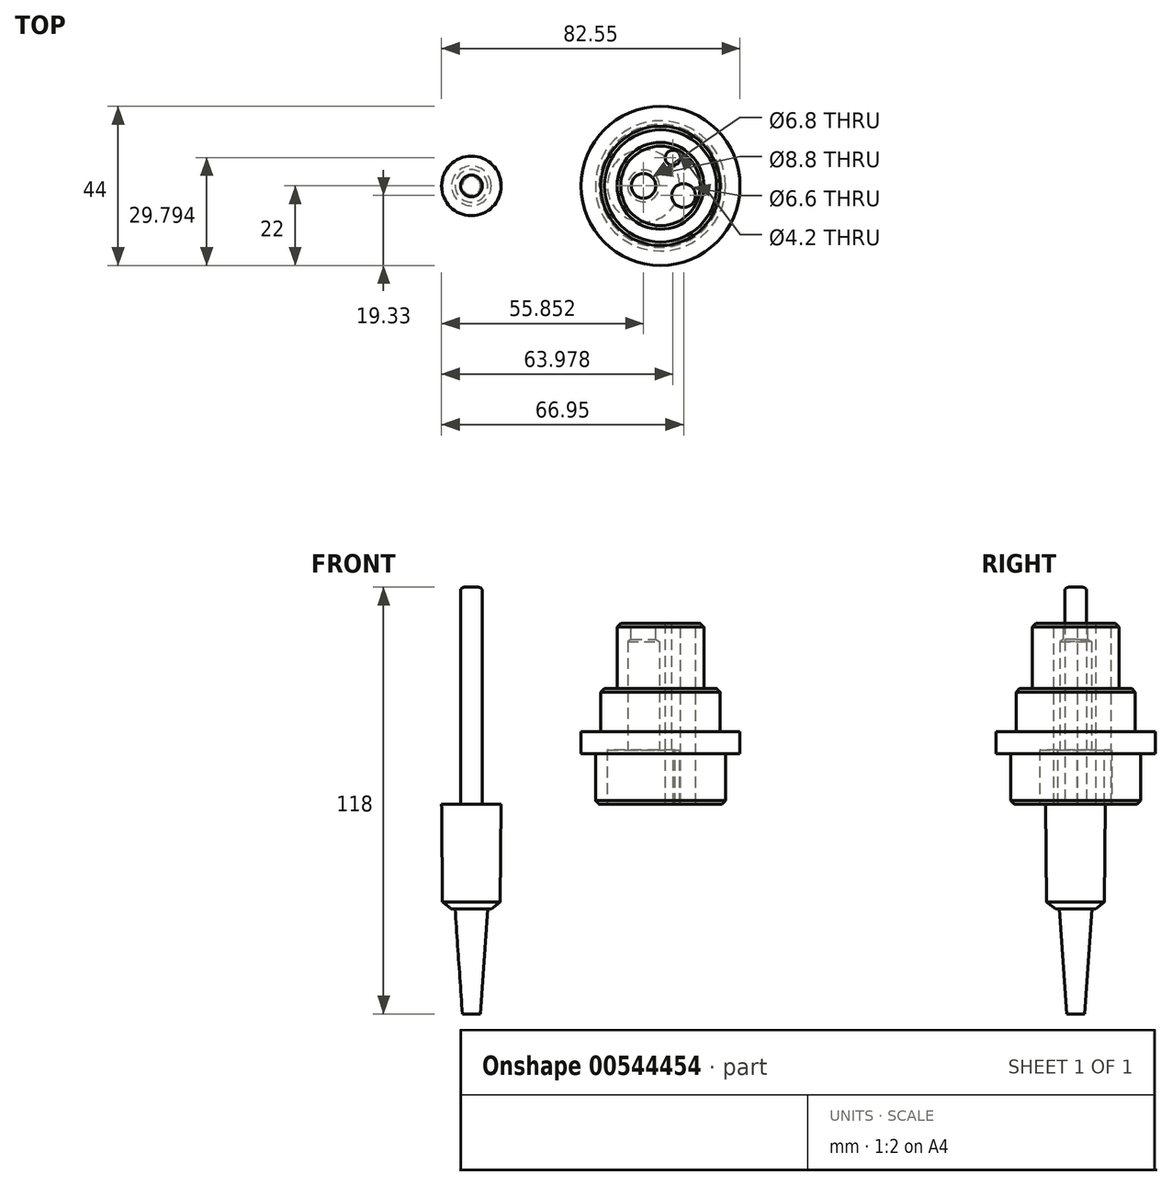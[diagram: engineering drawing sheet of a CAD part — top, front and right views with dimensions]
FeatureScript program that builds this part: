
annotation { "Feature Type Name" : "Feature", "Feature Type Description" : "" }
export const myFeature = defineFeature(function(context is Context, id is Id, definition is map)
    precondition{}
    {
        {
            var Q0;
            Q0=qCreatedBy(makeId("Top.planeOp"),FACE);
            var sketch = newSketch(context, id + "F0", { "sketchPlane" : qUnion([Q0])});
            skCircle(sketch, "E0", {"center": v(0, 0) * mm, "radius": 22 * mm});
            skSolve(sketch);
        }
        {
            var Q0;
            Q0 = qSketchRegion(id + "F0", true);
            extrude(context, id + "F1", {"entities" : qUnion([Q0]), "depth" : 6 * mm, "offsetDistance" : 25 * mm});
        }
        {
            var Q0;
            Q0=makeQuery(id+"F1.opExtrude","CAP_FACE",FACE,{"disambiguationData":[OSD([sQuery(id+"F0.wireOp",EDGE,"E0")])],"isStart":false});
            var sketch = newSketch(context, id + "F2", { "sketchPlane" : qUnion([Q0])});
            skCircle(sketch, "E1", {"center": v(0, 0) * mm, "radius": 16.5 * mm});
            skSolve(sketch);
        }
        {
            var Q0;
            Q0 = qSketchRegion(id + "F2", true);
            extrude(context, id + "F3", {"entities" : qUnion([Q0]), "operationType" : NewBodyOperationType.ADD, "depth" : 12 * mm, "offsetDistance" : 25 * mm});
        }
        {
            var Q0;
            Q0=makeQuery(id+"F3.opExtrude","CAP_FACE",FACE,{"disambiguationData":[OSD([sQuery(id+"F2.wireOp",EDGE,"E1")])],"isStart":false});
            var sketch = newSketch(context, id + "F4", { "sketchPlane" : qUnion([Q0])});
            skCircle(sketch, "E2", {"center": v(0, 0) * mm, "radius": 12 * mm});
            skSolve(sketch);
        }
        {
            var Q0;
            Q0 = qSketchRegion(id + "F4", true);
            extrude(context, id + "F5", {"entities" : qUnion([Q0]), "operationType" : NewBodyOperationType.ADD, "depth" : 18 * mm, "offsetDistance" : 25 * mm});
        }
        {
            var Q0;
            Q0=makeQuery(id+"F1.opExtrude","CAP_FACE",FACE,{"disambiguationData":[OSD([sQuery(id+"F0.wireOp",EDGE,"E0")])],"isStart":true});
            var sketch = newSketch(context, id + "F6", { "sketchPlane" : qUnion([Q0])});
            skCircle(sketch, "E3", {"center": v(0, 0) * mm, "radius": 18 * mm});
            skSolve(sketch);
        }
        {
            var Q0;
            Q0 = qSketchRegion(id + "F6", true);
            extrude(context, id + "F7", {"entities" : qUnion([Q0]), "operationType" : NewBodyOperationType.ADD, "depth" : 14 * mm, "offsetDistance" : 25 * mm});
        }
        {
            var Q0;
            Q0=makeQuery(id+"F7.opExtrude","CAP_EDGE",EDGE,{"disambiguationData":[OSD([sQuery(id+"F6.wireOp",EDGE,"E3")])],"isStart":false});
            var Q1;
            Q1=makeQuery(id+"F3.opExtrude","CAP_EDGE",EDGE,{"disambiguationData":[OSD([sQuery(id+"F2.wireOp",EDGE,"E1")])],"isStart":false});
            chamfer(context, id + "F8", {"entities" : qUnion([Q0, Q1]), "width" : 1 * mm, "tangentPropagation" : true});
        }
        {
            var Q0;
            Q0=makeQuery(id+"F5.opExtrude","CAP_EDGE",EDGE,{"disambiguationData":[OSD([sQuery(id+"F4.wireOp",EDGE,"E2")])],"isStart":false});
            chamfer(context, id + "F9", {"entities" : qUnion([Q0]), "width" : 1 * mm, "tangentPropagation" : true});
        }
        {
            var Q0;
            Q0=qCreatedBy(makeId("Front.planeOp"),FACE);
            var sketch = newSketch(context, id + "F10", { "sketchPlane" : qUnion([Q0])});
            skLineSegment(sketch, "E4", {"start": v(-65.3, -14) * mm, "end": v(-17, -14) * mm, "construction": true});
            skLineSegment(sketch, "E5", {"start": v(-52.3, 40.72) * mm, "end": v(-52.3, -49.75) * mm, "construction": true});
            skLineSegment(sketch, "E6", {"start": v(-44.05, -14) * mm, "end": v(-44.3, -41) * mm});
            skLineSegment(sketch, "E7", {"start": v(-52.3, -41.5) * mm, "end": v(-52.3, 46) * mm});
            skLineSegment(sketch, "E8", {"start": v(-52.3, 46) * mm, "end": v(-50.3, 46) * mm});
            skLineSegment(sketch, "E9", {"start": v(-49.3, 45) * mm, "end": v(-49.3, -14) * mm});
            skLineSegment(sketch, "E10", {"start": v(-49.3, -14) * mm, "end": v(-44.05, -14) * mm});
            skPoint(sketch, "E11.visualSharp", {"position": v(-49.3, 46) * mm});
            skArc(sketch, "E11.filletArc", {"start": v(-49.3, 45) * mm, "mid": v(-49.6, 45.7) * mm, "end": v(-50.3, 46) * mm});
            skLineSegment(sketch, "E12", {"start": v(-44.3, -41) * mm, "end": v(-46.8, -43) * mm});
            skLineSegment(sketch, "E13", {"start": v(-46.8, -43) * mm, "end": v(-47.8, -43) * mm});
            skLineSegment(sketch, "E14", {"start": v(-47.8, -43) * mm, "end": v(-49.8, -72) * mm});
            skLineSegment(sketch, "E15", {"start": v(-49.8, -72) * mm, "end": v(-52.3, -72) * mm});
            skLineSegment(sketch, "E16", {"start": v(-52.3, -41.5) * mm, "end": v(-52.3, -72) * mm});
            skSolve(sketch);
        }
        {
            var Q0;
            Q0=makeQuery(id+"F10.imprint","IMPRINT",FACE,{"disambiguationData":[TD([[makeQuery(id+"F10.imprint","IMPRINT",EDGE,{"derivedFrom":sQuery(id+"F10.wireOp",EDGE,"E6")}),-1.0]])]});
            var Q1;
            Q1=sQuery(id+"F10.wireOp",EDGE,"E7");
            revolve(context, id + "F11", {"entities" : qUnion([Q0]), "axis" : qUnion([Q1]), "revolveType" : RevolveType.FULL});
        }
        {
            var Q0;
            Q0=makeQuery(id+"F5.opExtrude","CAP_FACE",FACE,{"disambiguationData":[OSD([sQuery(id+"F4.wireOp",EDGE,"E2")])],"isStart":false});
            var sketch = newSketch(context, id + "F12", { "sketchPlane" : qUnion([Q0])});
            skPoint(sketch, "E17", {"position": v(-4.7, 0) * mm});
            skPoint(sketch, "E18", {"position": v(6.4, -2.67) * mm});
            skPoint(sketch, "E19", {"position": v(3.43, 7.8) * mm});
            skCircle(sketch, "E20", {"center": v(-4.7, 0) * mm, "radius": 6 * mm, "construction": true});
            skSolve(sketch);
        }
        {
            var Q0;
            Q0=makeQuery(id+"F7.opExtrude","CAP_FACE",FACE,{"disambiguationData":[OSD([sQuery(id+"F6.wireOp",EDGE,"E3")])],"isStart":false});
            var sketch = newSketch(context, id + "F13", { "sketchPlane" : qUnion([Q0])});
            skPoint(sketch, "E21.0", {"position": v(-4.7, 0) * mm});
            skPoint(sketch, "E22.0", {"position": v(3.43, -7.8) * mm});
            skPoint(sketch, "E23.0", {"position": v(6.4, 2.67) * mm});
            skCircle(sketch, "E24", {"center": v(6.4, 2.67) * mm, "radius": 8.25 * mm, "construction": true});
            skSolve(sketch);
        }
        {
            var Q0;
            Q0=sQuery(id+"F12.wireOp",VERTEX,"E17");
            var Q1;
            Q1=makeQuery(id+"F1.opExtrude","SWEPT_BODY",BODY,{"disambiguationData":[OSD([sQuery(id+"F0.wireOp",EDGE,"E0")])]});
            hole(context, id + "F14", {"style" : HoleStyle.SIMPLE, "endStyle" : HoleEndStyle.BLIND, "standardTappedOrClearance" : lookupTablePath({ "standard" : "ISO", "engagement" : "75%", "pitch" : "1.25 mm", "size" : "M8", "type" : "Tapped" }), "standardBlindInLast" : lookupTablePath({ "standard" : "ISO", "engagement" : "75%", "pitch" : "1.25 mm", "size" : "M8", "type" : "Tapped" }), "holeDiameter" : 6.8 * mm, "majorDiameter" : 8 * mm, "showTappedDepth" : true, "holeDepth" : 13.75 * mm, "isTappedThrough" : true, "tappedDepth" : 10 * mm, "tapClearance" : 3, "locations" : qUnion([Q0]), "scope" : qUnion([Q1])});
        }
        {
            var Q0;
            Q0=sQuery(id+"F13.wireOp",VERTEX,"E21.0");
            var Q1;
            Q1=makeQuery(id+"F1.opExtrude","SWEPT_BODY",BODY,{"disambiguationData":[OSD([sQuery(id+"F0.wireOp",EDGE,"E0")])]});
            hole(context, id + "F15", {"style" : HoleStyle.C_BORE, "endStyle" : HoleEndStyle.BLIND, "holeDiameter" : 8.8 * mm, "cBoreDiameter" : 20 * mm, "cBoreDepth" : 15 * mm, "majorDiameter" : 20 * mm, "holeDepth" : 45 * mm, "tappedDepth" : 3.6 * mm, "tapClearance" : 3, "locations" : qUnion([Q0]), "scope" : qUnion([Q1])});
        }
        {
            var Q0;
            Q0=sQuery(id+"F12.wireOp",VERTEX,"E18");
            var Q1;
            Q1=makeQuery(id+"F1.opExtrude","SWEPT_BODY",BODY,{"disambiguationData":[OSD([sQuery(id+"F0.wireOp",EDGE,"E0")])]});
            hole(context, id + "F16", {"style" : HoleStyle.SIMPLE, "endStyle" : HoleEndStyle.THROUGH, "standardTappedOrClearance" : lookupTablePath({ "standard" : "ISO", "fit" : "Normal", "size" : "M6", "type" : "Clearance" }), "standardBlindInLast" : lookupTablePath({ "fit" : "Standard", "standard" : "ISO", "size" : "M6", "type" : "Clearance" }), "holeDiameter" : 6.6 * mm, "majorDiameter" : 6 * mm, "tappedDepth" : 3.6 * mm, "tapClearance" : 3, "locations" : qUnion([Q0]), "scope" : qUnion([Q1])});
        }
        {
            var Q0;
            Q0=sQuery(id+"F12.wireOp",VERTEX,"E19");
            var Q1;
            Q1=makeQuery(id+"F1.opExtrude","SWEPT_BODY",BODY,{"disambiguationData":[OSD([sQuery(id+"F0.wireOp",EDGE,"E0")])]});
            hole(context, id + "F17", {"style" : HoleStyle.SIMPLE, "endStyle" : HoleEndStyle.THROUGH, "standardTappedOrClearance" : lookupTablePath({ "standard" : "ISO", "engagement" : "75%", "pitch" : "0.8 mm", "size" : "M5", "type" : "Tapped" }), "standardBlindInLast" : lookupTablePath({ "standard" : "ISO", "engagement" : "75%", "pitch" : "0.8 mm", "size" : "M5", "type" : "Tapped" }), "holeDiameter" : 4.2 * mm, "majorDiameter" : 5 * mm, "showTappedDepth" : true, "tappedDepth" : 3.6 * mm, "tapClearance" : 3, "locations" : qUnion([Q0]), "scope" : qUnion([Q1])});
        }
    });
